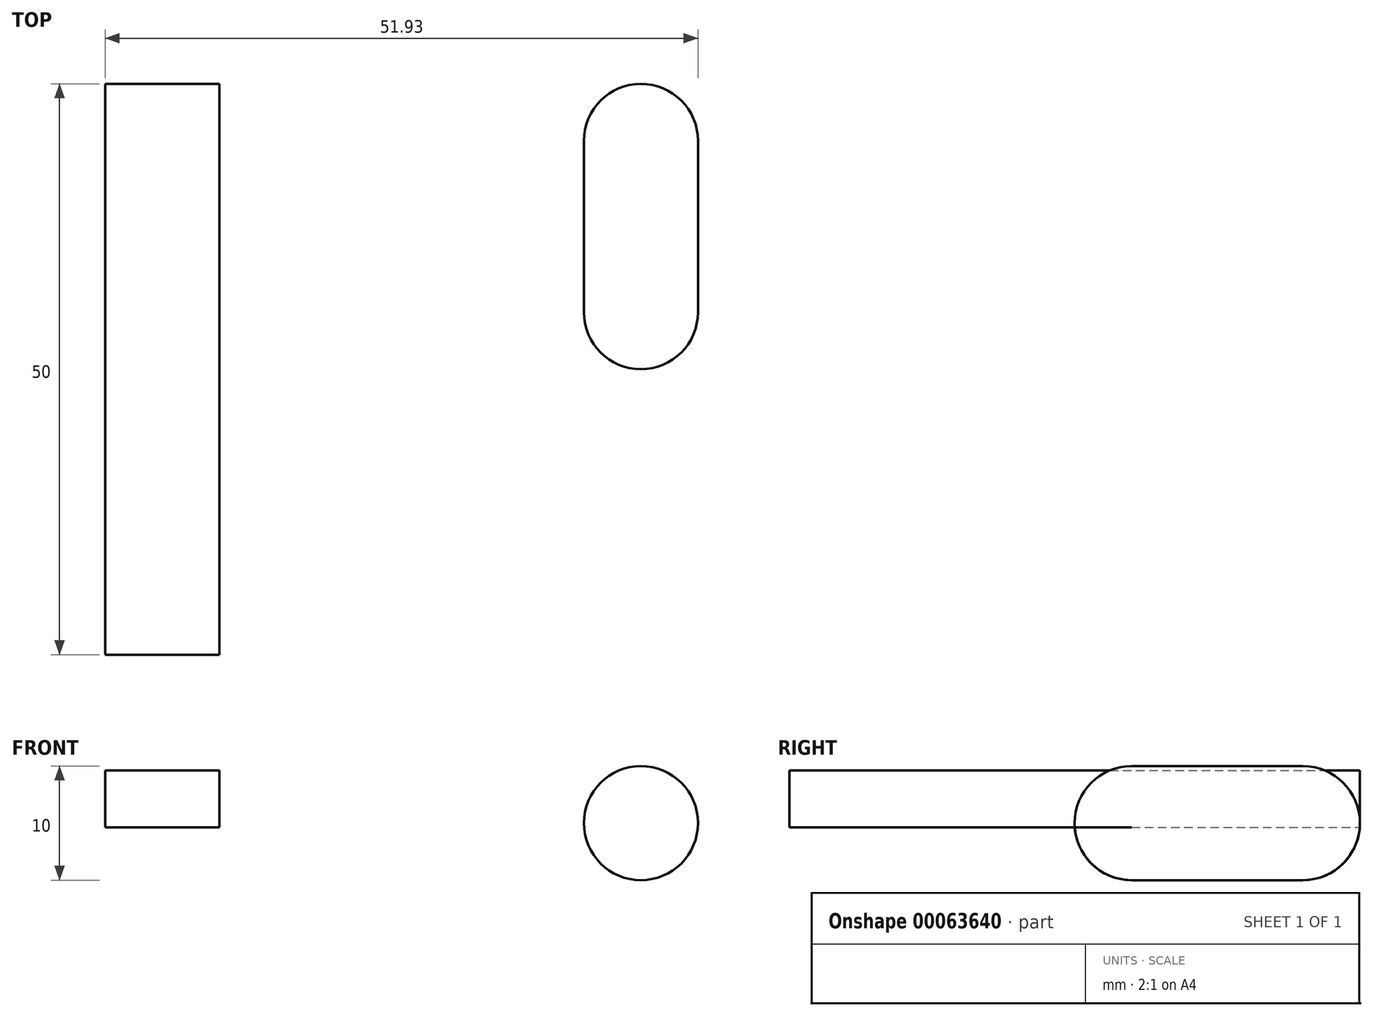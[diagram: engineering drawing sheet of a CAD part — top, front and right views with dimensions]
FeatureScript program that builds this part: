
annotation { "Feature Type Name" : "Feature", "Feature Type Description" : "" }
export const myFeature = defineFeature(function(context is Context, id is Id, definition is map)
    precondition{}
    {
        {
            var Q0;
            Q0=qCreatedBy(makeId("Front.planeOp"),FACE);
            var sketch = newSketch(context, id + "F0", { "sketchPlane" : qUnion([Q0])});
            skLineSegment(sketch, "E0.bottom", {"start": v(-33.96, 18.7) * mm, "end": v(-23.96, 18.7) * mm});
            skLineSegment(sketch, "E0.top", {"start": v(-33.96, 13.7) * mm, "end": v(-23.96, 13.7) * mm});
            skLineSegment(sketch, "E0.left", {"start": v(-33.96, 18.7) * mm, "end": v(-33.96, 13.7) * mm});
            skLineSegment(sketch, "E0.right", {"start": v(-23.96, 18.7) * mm, "end": v(-23.96, 13.7) * mm});
            skSolve(sketch);
        }
        {
            var Q0;
            Q0 = qSketchRegion(id + "F0", true);
            extrude(context, id + "F1", {"entities" : qUnion([Q0]), "depth" : 50 * mm});
        }
        {
            var Q0;
            Q0=qCreatedBy(makeId("Front.planeOp"),FACE);
            var sketch = newSketch(context, id + "F2", { "sketchPlane" : qUnion([Q0])});
            skCircle(sketch, "E1", {"center": v(12.97, 14.09) * mm, "radius": 5 * mm});
            skSolve(sketch);
        }
        {
            var Q0;
            Q0 = qSketchRegion(id + "F2", true);
            extrude(context, id + "F3", {"entities" : qUnion([Q0]), "depth" : 25 * mm});
        }
        {
            var Q0;
            Q0=makeQuery(id+"F3.opExtrude","CAP_FACE",FACE,{"disambiguationData":[OSD([sQuery(id+"F2.wireOp",EDGE,"E1")])],"isStart":false});
            var Q1;
            Q1=makeQuery(id+"F3.opExtrude","CAP_FACE",FACE,{"disambiguationData":[OSD([sQuery(id+"F2.wireOp",EDGE,"E1")])],"isStart":true});
            fillet(context, id + "F4", {"entities" : qUnion([Q0, Q1]), "radius" : 5 * mm, "tangentPropagation" : true, "allowEdgeOverflow" : false});
        }
    });
